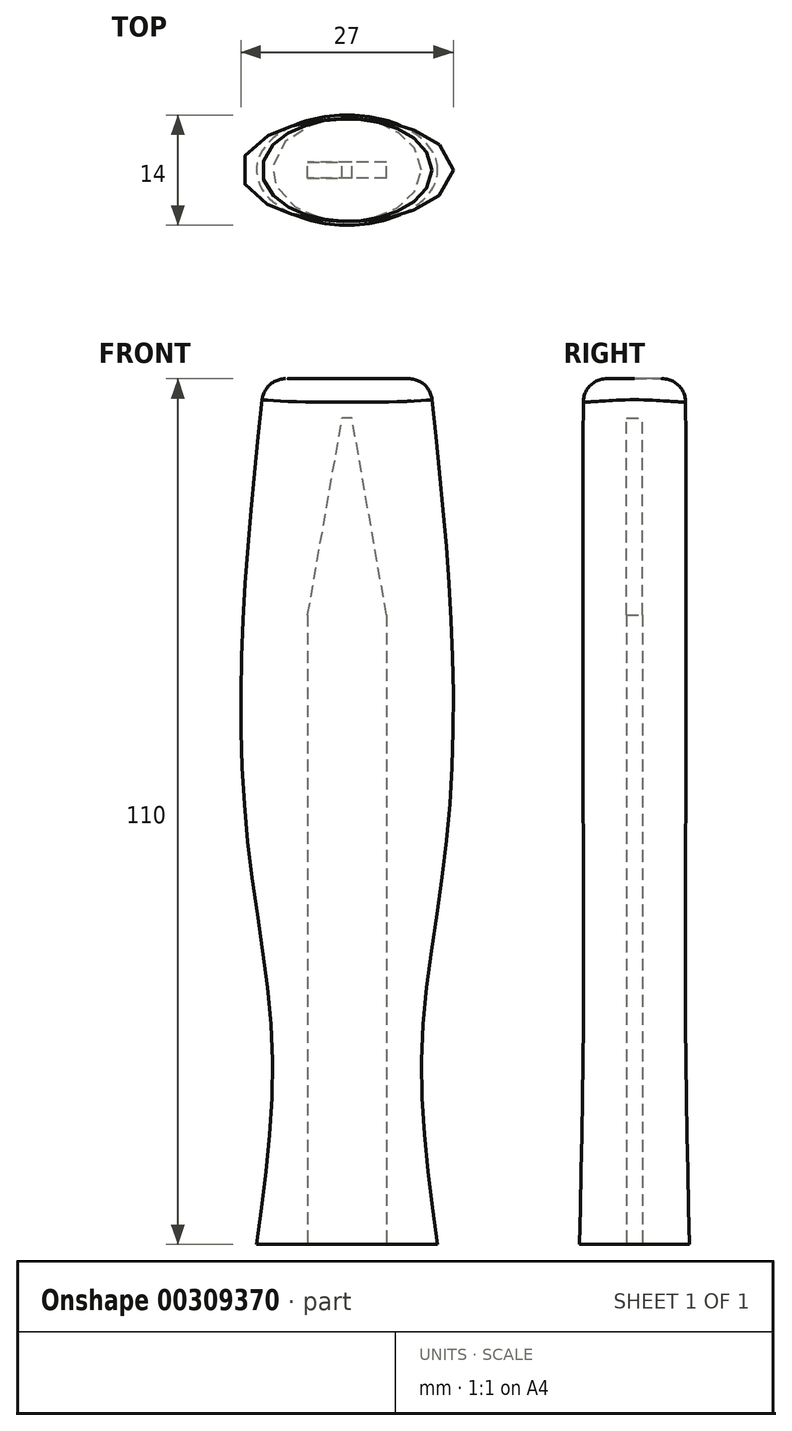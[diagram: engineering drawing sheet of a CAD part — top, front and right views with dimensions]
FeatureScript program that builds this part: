
annotation { "Feature Type Name" : "Feature", "Feature Type Description" : "" }
export const myFeature = defineFeature(function(context is Context, id is Id, definition is map)
    precondition{}
    {
        {
            var Q0;
            Q0=qCreatedBy(makeId("Top.planeOp"),FACE);
            cPlane(context, id + "F0", {"entities" : qUnion([Q0]), "cplaneType" : CPlaneType.OFFSET, "offset" : 25 * mm, "width" : 150 * mm, "height" : 150 * mm});
        }
        {
            var Q0;
            Q0=qCreatedBy(id+"F0.planeOp",FACE);
            cPlane(context, id + "F1", {"entities" : qUnion([Q0]), "cplaneType" : CPlaneType.OFFSET, "offset" : 25 * mm, "width" : 150 * mm, "height" : 150 * mm});
        }
        {
            var Q0;
            Q0=qCreatedBy(id+"F1.planeOp",FACE);
            cPlane(context, id + "F2", {"entities" : qUnion([Q0]), "cplaneType" : CPlaneType.OFFSET, "offset" : 60 * mm, "width" : 150 * mm, "height" : 150 * mm});
        }
        {
            var Q0;
            Q0=qCreatedBy(id+"F1.planeOp",FACE);
            cPlane(context, id + "F3", {"entities" : qUnion([Q0]), "cplaneType" : CPlaneType.OFFSET, "offset" : 55 * mm, "width" : 150 * mm, "height" : 150 * mm});
        }
        {
            var Q0;
            Q0=qCreatedBy(makeId("Top.planeOp"),FACE);
            cPlane(context, id + "F4", {"entities" : qUnion([Q0]), "cplaneType" : CPlaneType.OFFSET, "offset" : 80 * mm, "width" : 150 * mm, "height" : 150 * mm});
        }
        {
            var Q0;
            Q0=qCreatedBy(makeId("Top.planeOp"),FACE);
            var sketch = newSketch(context, id + "F5", { "sketchPlane" : qUnion([Q0])});
            skEllipse(sketch, "E0", {"center": v(0, 0) * mm, "majorRadius": 11.5 * mm, "minorRadius": 7 * mm, "majorAxis": v(1, 0)});
            skSolve(sketch);
        }
        {
            var Q0;
            Q0=qCreatedBy(id+"F0.planeOp",FACE);
            var sketch = newSketch(context, id + "F6", { "sketchPlane" : qUnion([Q0])});
            skEllipse(sketch, "E1", {"center": v(0, 0) * mm, "majorRadius": 9.5 * mm, "minorRadius": 6.5 * mm, "majorAxis": v(1, 0)});
            skSolve(sketch);
        }
        {
            var Q0;
            Q0=qCreatedBy(id+"F1.planeOp",FACE);
            var sketch = newSketch(context, id + "F7", { "sketchPlane" : qUnion([Q0])});
            skEllipse(sketch, "E2", {"center": v(0, 0) * mm, "majorRadius": 12.5 * mm, "minorRadius": 6.5 * mm, "majorAxis": v(1, 0)});
            skSolve(sketch);
        }
        {
            var Q0;
            Q0=qCreatedBy(id+"F2.planeOp",FACE);
            var sketch = newSketch(context, id + "F8", { "sketchPlane" : qUnion([Q0])});
            skEllipse(sketch, "E3", {"center": v(0, 0) * mm, "majorRadius": 10.5 * mm, "minorRadius": 6.5 * mm, "majorAxis": v(1, 0)});
            skSolve(sketch);
        }
        {
            var Q0;
            Q0=qSketchRegion(id+"F5",true);
            var Q1;
            Q1=qSketchRegion(id+"F6",true);
            var Q2;
            Q2=qSketchRegion(id+"F7",true);
            var Q3;
            Q3=qSketchRegion(id+"F8",true);
            loft(context, id + "F9", {"sheetProfilesArray" : [{ "sheetProfileEntities" : qUnion([Q0]) }, { "sheetProfileEntities" : qUnion([Q1]) }, { "sheetProfileEntities" : qUnion([Q2]) }, { "sheetProfileEntities" : qUnion([Q3]) }]});
        }
        {
            var Q0;
            Q0=qCreatedBy(makeId("Top.planeOp"),FACE);
            var sketch = newSketch(context, id + "F10", { "sketchPlane" : qUnion([Q0])});
            skLineSegment(sketch, "E4.bottom", {"start": v(5, -1) * mm, "end": v(-5, -1) * mm});
            skLineSegment(sketch, "E4.top", {"start": v(5, 1) * mm, "end": v(-5, 1) * mm});
            skLineSegment(sketch, "E4.left", {"start": v(5, -1) * mm, "end": v(5, 1) * mm});
            skLineSegment(sketch, "E4.right", {"start": v(-5, -1) * mm, "end": v(-5, 1) * mm});
            skPoint(sketch, "E4.middle", {"position": v(0, 0) * mm});
            skSolve(sketch);
        }
        {
            var Q0;
            Q0=qCreatedBy(id+"F4.planeOp",FACE);
            var sketch = newSketch(context, id + "F11", { "sketchPlane" : qUnion([Q0])});
            skLineSegment(sketch, "E5.0", {"start": v(5, 1) * mm, "end": v(-5, 1) * mm});
            skPoint(sketch, "E6.0", {"position": v(-5, 0) * mm});
            skLineSegment(sketch, "E7.0", {"start": v(-5, -1) * mm, "end": v(-5, 1) * mm});
            skLineSegment(sketch, "E8.0", {"start": v(5, -1) * mm, "end": v(-5, -1) * mm});
            skLineSegment(sketch, "E9.0", {"start": v(5, -1) * mm, "end": v(5, 1) * mm});
            skSolve(sketch);
        }
        {
            var Q0;
            Q0=qCreatedBy(id+"F3.planeOp",FACE);
            var sketch = newSketch(context, id + "F12", { "sketchPlane" : qUnion([Q0])});
            skLineSegment(sketch, "E10.bottom", {"start": v(0.62, -1) * mm, "end": v(-0.62, -1) * mm});
            skLineSegment(sketch, "E10.top", {"start": v(0.62, 1) * mm, "end": v(-0.62, 1) * mm});
            skLineSegment(sketch, "E10.left", {"start": v(0.62, -1) * mm, "end": v(0.62, 1) * mm});
            skLineSegment(sketch, "E10.right", {"start": v(-0.62, -1) * mm, "end": v(-0.62, 1) * mm});
            skPoint(sketch, "E10.middle", {"position": v(0, 0) * mm});
            skSolve(sketch);
        }
        {
            var Q0;
            Q0=qSketchRegion(id+"F10",true);
            extrude(context, id + "F13", {"entities" : qUnion([Q0]), "operationType" : NewBodyOperationType.REMOVE, "depth" : 80 * mm});
        }
        {
            var Q1;
            Q1=qSketchRegion(id+"F11",true);
            var Q2;
            Q2=qSketchRegion(id+"F12",true);
            loft(context, id + "F14", {"operationType" : NewBodyOperationType.REMOVE, "sheetProfilesArray" : [{ "sheetProfileEntities" : qUnion([Q1]) }, { "sheetProfileEntities" : qUnion([Q2]) }]});
        }
        {
            var Q0;
            Q0=makeQuery(id+"F9.opLoft","MID_CAP_EDGE",EDGE,{"disambiguationData":[OSD([sQuery(id+"F5.wireOp",EDGE,"E0"),sQuery(id+"F8.wireOp",EDGE,"E3")])],"capPos":3.0});
            fillet(context, id + "F15", {"entities" : qUnion([Q0]), "radius" : 3 * mm, "tangentPropagation" : true, "allowEdgeOverflow" : false});
        }
    });
